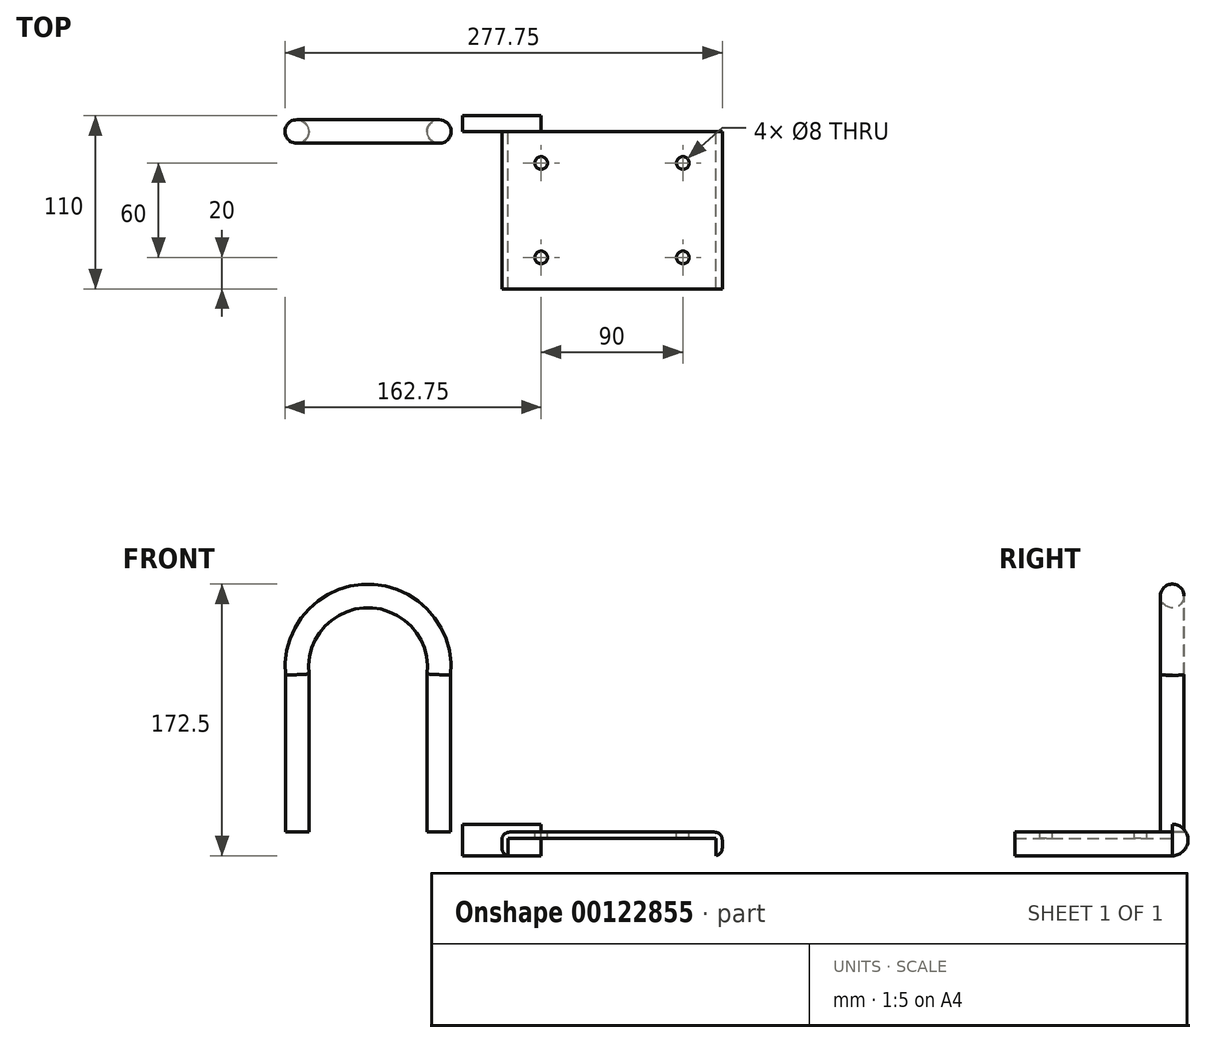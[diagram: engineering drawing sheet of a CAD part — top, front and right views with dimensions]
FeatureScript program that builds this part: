
annotation { "Feature Type Name" : "Feature", "Feature Type Description" : "" }
export const myFeature = defineFeature(function(context is Context, id is Id, definition is map)
    precondition{}
    {
        {
            var Q0;
            Q0=qCreatedBy(makeId("Front.planeOp"),FACE);
            var sketch = newSketch(context, id + "F0", { "sketchPlane" : qUnion([Q0])});
            skLineSegment(sketch, "E0", {"start": v(0, 0) * mm, "end": v(140, 0) * mm});
            skLineSegment(sketch, "E1", {"start": v(140, 0) * mm, "end": v(140, -15) * mm});
            skLineSegment(sketch, "E2", {"start": v(0, 0) * mm, "end": v(0, -15) * mm});
            skLineSegment(sketch, "E3", {"start": v(0, -15) * mm, "end": v(4, -15) * mm});
            skLineSegment(sketch, "E4", {"start": v(4, -15) * mm, "end": v(4, -4) * mm});
            skLineSegment(sketch, "E5", {"start": v(140, -15) * mm, "end": v(136, -15) * mm});
            skLineSegment(sketch, "E6", {"start": v(136, -15) * mm, "end": v(136, -4) * mm});
            skLineSegment(sketch, "E7", {"start": v(136, -4) * mm, "end": v(4, -4) * mm});
            skSolve(sketch);
        }
        {
            var Q0;
            Q0 = qSketchRegion(id + "F0", true);
            extrude(context, id + "F1", {"entities" : qUnion([Q0]), "depth" : 100 * mm});
        }
        {
            var Q0;
            Q0=makeQuery(id+"F1.opExtrude","SWEPT_EDGE",EDGE,{"disambiguationData":[OSD([sQuery(id+"F0.wireOp",EDGE,"E0"),sQuery(id+"F0.wireOp",EDGE,"E2")])]});
            var Q1;
            Q1=makeQuery(id+"F1.opExtrude","SWEPT_EDGE",EDGE,{"disambiguationData":[OSD([sQuery(id+"F0.wireOp",EDGE,"E1"),sQuery(id+"F0.wireOp",EDGE,"E5")])]});
            fillet(context, id + "F2", {"entities" : qUnion([Q0, Q1]), "radius" : 5 * mm, "tangentPropagation" : true, "allowEdgeOverflow" : false});
        }
        {
            var Q0;
            Q0=makeQuery(id+"F1.opExtrude","SWEPT_EDGE",EDGE,{"disambiguationData":[OSD([sQuery(id+"F0.wireOp",EDGE,"E2"),sQuery(id+"F0.wireOp",EDGE,"E3")])]});
            var Q1;
            Q1=makeQuery(id+"F1.opExtrude","SWEPT_EDGE",EDGE,{"disambiguationData":[OSD([sQuery(id+"F0.wireOp",EDGE,"E0"),sQuery(id+"F0.wireOp",EDGE,"E1")])]});
            fillet(context, id + "F3", {"entities" : qUnion([Q0, Q1]), "radius" : 5 * mm, "tangentPropagation" : true, "allowEdgeOverflow" : false});
        }
        {
            var Q0;
            Q0=makeQuery(id+"F1.opExtrude","SWEPT_FACE",FACE,{"disambiguationData":[OSD([sQuery(id+"F0.wireOp",EDGE,"E0")])]});
            var sketch = newSketch(context, id + "F4", { "sketchPlane" : qUnion([Q0])});
            skLineSegment(sketch, "E8.0", {"start": v(5, 0) * mm, "end": v(70, 0) * mm, "construction": true});
            skLineSegment(sketch, "E9", {"start": v(70, 0) * mm, "end": v(70, -100) * mm, "construction": true});
            skLineSegment(sketch, "E10", {"start": v(70, -50) * mm, "end": v(70, -20) * mm, "construction": true});
            skLineSegment(sketch, "E11", {"start": v(70, -20) * mm, "end": v(25, -20) * mm, "construction": true});
            skLineSegment(sketch, "E12", {"start": v(70, -20) * mm, "end": v(115, -20) * mm, "construction": true});
            skLineSegment(sketch, "E13", {"start": v(25, -20) * mm, "end": v(25, -80) * mm, "construction": true});
            skLineSegment(sketch, "E14", {"start": v(25, -80) * mm, "end": v(115, -80) * mm, "construction": true});
            skPoint(sketch, "E15", {"position": v(25, -20) * mm});
            skPoint(sketch, "E16", {"position": v(115, -20) * mm});
            skPoint(sketch, "E17", {"position": v(25, -80) * mm});
            skPoint(sketch, "E18", {"position": v(115, -80) * mm});
            skLineSegment(sketch, "E19", {"start": v(70, 10) * mm, "end": v(70, 0) * mm});
            skLineSegment(sketch, "E20", {"start": v(70, 0) * mm, "end": v(70, -1) * mm});
            skLineSegment(sketch, "E21", {"start": v(70, -1) * mm, "end": v(135, -1) * mm});
            skLineSegment(sketch, "E22", {"start": v(135, -1) * mm, "end": v(165, -1) * mm});
            skLineSegment(sketch, "E23", {"start": v(165, -1) * mm, "end": v(165, 10) * mm});
            skLineSegment(sketch, "E24", {"start": v(70, 10) * mm, "end": v(165, 10) * mm});
            skSolve(sketch);
        }
        {
            var Q0;
            Q0=sQuery(id+"F4.wireOp",VERTEX,"E15");
            var Q1;
            Q1=sQuery(id+"F4.wireOp",VERTEX,"E16");
            var Q2;
            Q2=sQuery(id+"F4.wireOp",VERTEX,"E17");
            var Q3;
            Q3=sQuery(id+"F4.wireOp",VERTEX,"E18");
            var Q4;
            Q4=makeQuery(id+"F1.opExtrude","SWEPT_BODY",BODY,{"disambiguationData":[OSD([sQuery(id+"F0.wireOp",EDGE,"E0"),sQuery(id+"F0.wireOp",EDGE,"E1"),sQuery(id+"F0.wireOp",EDGE,"E2"),sQuery(id+"F0.wireOp",EDGE,"E3"),sQuery(id+"F0.wireOp",EDGE,"E4"),sQuery(id+"F0.wireOp",EDGE,"E5"),sQuery(id+"F0.wireOp",EDGE,"E6"),sQuery(id+"F0.wireOp",EDGE,"E7")])]});
            hole(context, id + "F5", {"style" : HoleStyle.SIMPLE, "endStyle" : HoleEndStyle.THROUGH, "holeDiameter" : 8 * mm, "locations" : qUnion([Q0, Q1, Q2, Q3]), "scope" : qUnion([Q4]), "isTappedThrough" : true});
        }
        {
            var Q0;
            Q0=qCreatedBy(makeId("Front.planeOp"),FACE);
            var sketch = newSketch(context, id + "F6", { "sketchPlane" : qUnion([Q0])});
            skLineSegment(sketch, "E25", {"start": v(0, 0) * mm, "end": v(-40, 0) * mm, "construction": true});
            skLineSegment(sketch, "E26", {"start": v(-85, 0) * mm, "end": v(-85, 150) * mm, "construction": true});
            skPoint(sketch, "E26.endSnap0", {"position": v(-85, 0) * mm});
            skLineSegment(sketch, "E27", {"start": v(-130, 100) * mm, "end": v(-130, 0) * mm});
            skLineSegment(sketch, "E28", {"start": v(-40, 0) * mm, "end": v(-40, 100) * mm});
            skArc(sketch, "E29", {"start": v(-40, 100) * mm, "mid": v(-85, 150) * mm, "end": v(-130, 100) * mm});
            skLineSegment(sketch, "E30", {"start": v(-85, 150) * mm, "end": v(-85, 135) * mm, "construction": true});
            skPoint(sketch, "E31.orphan", {"position": v(-145, 100) * mm});
            skPoint(sketch, "E32.end.orphan", {"position": v(-55, 100) * mm});
            skLineSegment(sketch, "E33", {"start": v(-130, 0) * mm, "end": v(-40, 0) * mm, "construction": true});
            skSolve(sketch);
        }
        {
            var Q0;
            Q0=qCreatedBy(makeId("Top.planeOp"),FACE);
            var sketch = newSketch(context, id + "F7", { "sketchPlane" : qUnion([Q0])});
            skLineSegment(sketch, "E34", {"start": v(0, 0) * mm, "end": v(-40, 0) * mm, "construction": true});
            skCircle(sketch, "E35", {"center": v(-40, 0) * mm, "radius": 7.5 * mm});
            skSolve(sketch);
        }
        {
            var Q0;
            Q0=makeQuery(id+"F7.imprint","IMPRINT",FACE,{"disambiguationData":[TD([[makeQuery(id+"F7.imprint","IMPRINT",EDGE,{"derivedFrom":sQuery(id+"F7.wireOp",EDGE,"E35")}),1.0]])]});
            var Q1;
            Q1=sQuery(id+"F7.wireOp",EDGE,"E35");
            var Q2;
            Q2=sQuery(id+"F6.wireOp",EDGE,"E28");
            var Q3;
            Q3=sQuery(id+"F6.wireOp",EDGE,"E29");
            var Q4;
            Q4=sQuery(id+"F6.wireOp",EDGE,"E27");
            sweep(context, id + "F8", {"profiles" : qUnion([Q0]), "surfaceProfiles" : qUnion([Q1]), "path" : qUnion([Q2, Q3, Q4])});
        }
        {
            var Q0;
            Q0=qCreatedBy(makeId("Right.planeOp"),FACE);
            var sketch = newSketch(context, id + "F9", { "sketchPlane" : qUnion([Q0])});
            skLineSegment(sketch, "E36.0", {"start": v(0, 0) * mm, "end": v(0, -5) * mm});
            skArc(sketch, "E37", {"start": v(0, -15) * mm, "mid": v(10, -5) * mm, "end": v(0, 5) * mm});
            skLineSegment(sketch, "E38", {"start": v(0, 0) * mm, "end": v(0, 5) * mm});
            skLineSegment(sketch, "E39", {"start": v(0, -5) * mm, "end": v(0, -15) * mm});
            skSolve(sketch);
        }
        {
            var Q0;
            Q0 = qSketchRegion(id + "F9", true);
            extrude(context, id + "F10", {"entities" : qUnion([Q0]), "operationType" : NewBodyOperationType.ADD, "endBound" : BoundingType.SYMMETRIC, "depth" : 50 * mm});
        }
    });
